# Revit family: SLH-Series Parallel Chord Bar Joist
name_source: partatom
category: Structural Framing
revit_build: Autodesk Revit Architecture 2012 (Build: 20110210_1515)
units: mm (PartAtom-declared; Revit-internal decimal feet)

## types (36) — shared parameters
Assembly Code = B1010350
Chord Thickness = 0' - 0 1/2"
Cord Leg = 0' - 2 1/2"
Rendering Material = <By Category>
Seat Depth = 0' - 7 1/2"
Seat Length = 0' - 6"
Web Thickness = 0' - 1"

## per-type parameters (varying)
| type | Depth | End Panel | Wt |
| 80SLH15 | 6' - 8" | 10' - 0" | 40 |
| 80SLH16 | 6' - 8" | 10' - 0" | 46 |
| 80SLH17 | 6' - 8" | 10' - 0" | 53 |
| 80SLH18 | 6' - 8" | 10' - 0" | 60 |
| 80SLH19 | 6' - 8" | 10' - 0" | 67 |
| 80SLH20 | 6' - 8" | 10' - 0" | 75 |
| 88SLH16 | 7' - 4" | 11' - 0" | 46 |
| 88SLH17 | 7' - 4" | 11' - 0" | 51 |
| 88SLH18 | 7' - 4" | 11' - 0" | 58 |
| 88SLH19 | 7' - 4" | 11' - 0" | 65 |
| 88SLH20 | 7' - 4" | 11' - 0" | 76 |
| 88SLH21 | 7' - 4" | 11' - 0" | 89 |
| 96SLH17 | 8' - 0" | 12' - 0" | 52 |
| 96SLH18 | 8' - 0" | 12' - 0" | 58 |
| 96SLH19 | 8' - 0" | 12' - 0" | 66 |
| 96SLH20 | 8' - 0" | 12' - 0" | 74 |
| 96SLH21 | 8' - 0" | 12' - 0" | 90 |
| 96SLH22 | 8' - 0" | 12' - 0" | 102 |
| 104SLH18 | 8' - 8" | 13' - 0" | 59 |
| 104SLH19 | 8' - 8" | 13' - 0" | 67 |
| 104SLH20 | 8' - 8" | 13' - 0" | 75 |
| 104SLH21 | 8' - 8" | 13' - 0" | 90 |
| 104SLH22 | 8' - 8" | 13' - 0" | 104 |
| 104SLH23 | 8' - 8" | 13' - 0" | 109 |
| 112LSH19 | 9' - 4" | 14' - 0" | 67 |
| 112SLH20 | 9' - 4" | 14' - 0" | 76 |
| 112SLH21 | 9' - 4" | 14' - 0" | 91 |
| 112SLH22 | 9' - 4" | 14' - 0" | 104 |
| 112SLH23 | 9' - 4" | 14' - 0" | 110 |
| 112SLH24 | 9' - 4" | 14' - 0" | 131 |
| 120SLH20 | 10' - 0" | 15' - 0" | 77 |
| 120SLH21 | 10' - 0" | 15' - 0" | 92 |
| 120SLH22 | 10' - 0" | 15' - 0" | 104 |
| 120SLH23 | 10' - 0" | 15' - 0" | 111 |
| 120SLH24 | 10' - 0" | 15' - 0" | 132 |
| 120SLH25 | 10' - 0" | 15' - 0" | 152 |

## geometry (parser evidence)
native form markers: Sweep x6
no freeform markers — native parametric forms only
